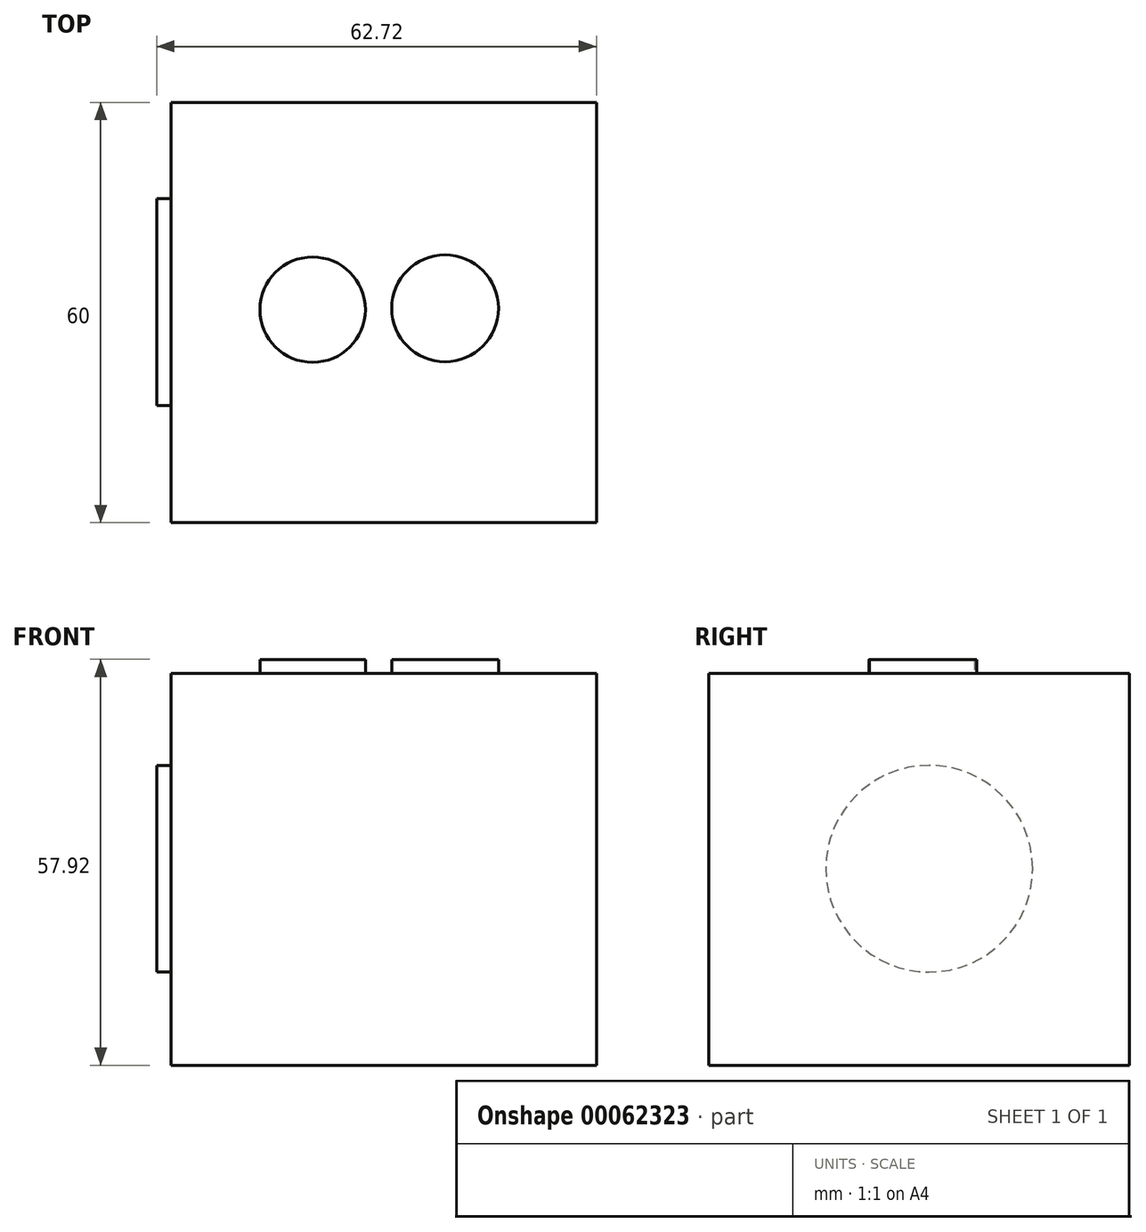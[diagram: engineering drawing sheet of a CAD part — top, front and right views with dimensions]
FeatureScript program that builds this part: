
annotation { "Feature Type Name" : "Feature", "Feature Type Description" : "" }
export const myFeature = defineFeature(function(context is Context, id is Id, definition is map)
    precondition{}
    {
        {
            var Q0;
            Q0=qCreatedBy(makeId("Front.planeOp"),FACE);
            var sketch = newSketch(context, id + "F0", { "sketchPlane" : qUnion([Q0])});
            skLineSegment(sketch, "E0.bottom", {"start": v(0, 0) * mm, "end": v(-60.72, 0) * mm});
            skLineSegment(sketch, "E0.top", {"start": v(0, 55.92) * mm, "end": v(-60.72, 55.92) * mm});
            skLineSegment(sketch, "E0.left", {"start": v(0, 0) * mm, "end": v(0, 55.92) * mm});
            skLineSegment(sketch, "E0.right", {"start": v(-60.72, 0) * mm, "end": v(-60.72, 55.92) * mm});
            skCircle(sketch, "E1", {"center": v(-31.14, 29.48) * mm, "radius": 7.6 * mm});
            skSolve(sketch);
        }
        {
            var Q0;
            Q0=makeQuery(id+"F0.imprint","IMPRINT",FACE,{"disambiguationData":[TD([[makeQuery(id+"F0.imprint","IMPRINT",EDGE,{"derivedFrom":sQuery(id+"F0.wireOp",EDGE,"E0.bottom")}),-1.0]])]});
            var Q1;
            Q1=makeQuery(id+"F0.imprint","IMPRINT",FACE,{"disambiguationData":[TD([[makeQuery(id+"F0.imprint","IMPRINT",EDGE,{"derivedFrom":sQuery(id+"F0.wireOp",EDGE,"E1")}),1.0]])]});
            extrude(context, id + "F1", {"entities" : qUnion([Q0, Q1]), "depth" : 60 * mm});
        }
        {
            var Q0;
            Q0=makeQuery(id+"F1.opExtrude","SWEPT_FACE",FACE,{"disambiguationData":[OSD([sQuery(id+"F0.wireOp",EDGE,"E0.right")])]});
            var sketch = newSketch(context, id + "F2", { "sketchPlane" : qUnion([Q0])});
            skCircle(sketch, "E2", {"center": v(28.53, 28.05) * mm, "radius": 14.75 * mm});
            skSolve(sketch);
        }
        {
            var Q0;
            Q0=makeQuery(id+"F2.imprint","IMPRINT",FACE,{"disambiguationData":[TD([[makeQuery(id+"F2.imprint","IMPRINT",EDGE,{"derivedFrom":sQuery(id+"F2.wireOp",EDGE,"E2")}),1.0]])]});
            extrude(context, id + "F3", {"entities" : qUnion([Q0]), "operationType" : NewBodyOperationType.ADD, "depth" : 2 * mm});
        }
        {
            var Q0;
            Q0=makeQuery(id+"F1.opExtrude","SWEPT_FACE",FACE,{"disambiguationData":[OSD([sQuery(id+"F0.wireOp",EDGE,"E0.top")])]});
            var sketch = newSketch(context, id + "F4", { "sketchPlane" : qUnion([Q0])});
            skCircle(sketch, "E3", {"center": v(-40.48, -29.6) * mm, "radius": 7.52 * mm});
            skSolve(sketch);
        }
        {
            var Q0;
            Q0=makeQuery(id+"F4.imprint","IMPRINT",FACE,{"disambiguationData":[TD([[makeQuery(id+"F4.imprint","IMPRINT",EDGE,{"derivedFrom":sQuery(id+"F4.wireOp",EDGE,"E3")}),-1.0]])]});
            var sketch = newSketch(context, id + "F5", { "sketchPlane" : qUnion([Q0])});
            skCircle(sketch, "E4", {"center": v(-21.6, -29.4) * mm, "radius": 7.63 * mm});
            skSolve(sketch);
        }
        {
            var Q0;
            Q0=makeQuery(id+"F4.imprint","IMPRINT",FACE,{"disambiguationData":[TD([[makeQuery(id+"F4.imprint","IMPRINT",EDGE,{"derivedFrom":sQuery(id+"F4.wireOp",EDGE,"E3")}),1.0]])]});
            extrude(context, id + "F6", {"entities" : qUnion([Q0]), "operationType" : NewBodyOperationType.ADD, "depth" : 2 * mm});
        }
        {
            var Q0;
            Q0=makeQuery(id+"F5.imprint","IMPRINT",FACE,{"disambiguationData":[TD([[makeQuery(id+"F5.imprint","IMPRINT",EDGE,{"derivedFrom":sQuery(id+"F5.wireOp",EDGE,"E4")}),1.0]])]});
            extrude(context, id + "F7", {"entities" : qUnion([Q0]), "operationType" : NewBodyOperationType.ADD, "depth" : 2 * mm});
        }
    });
